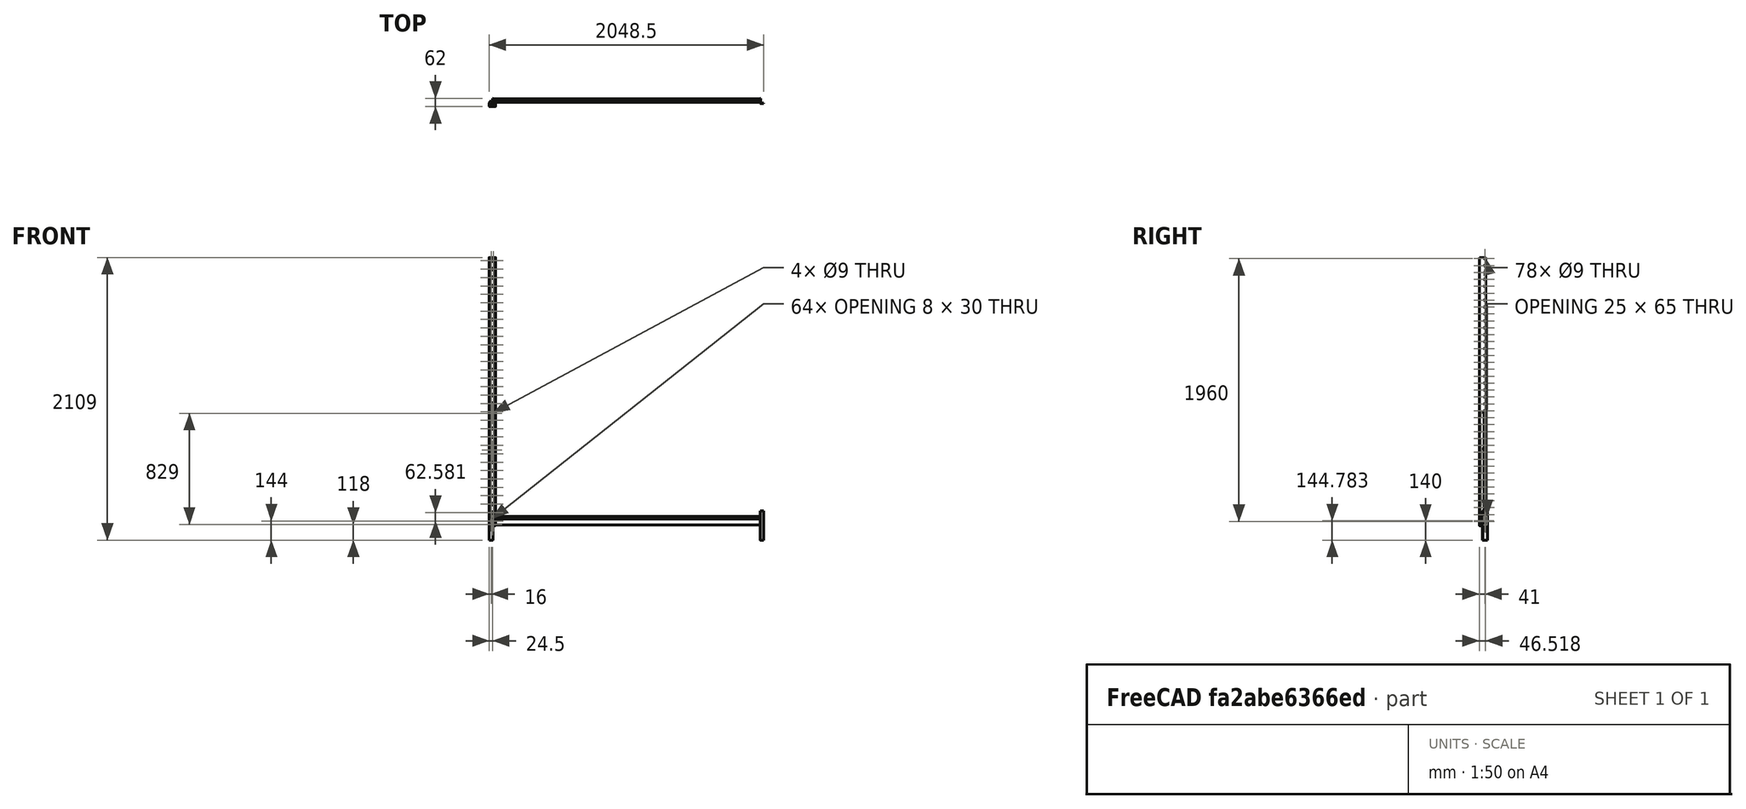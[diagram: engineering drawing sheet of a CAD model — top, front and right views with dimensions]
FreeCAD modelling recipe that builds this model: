
FCSTD DOCUMENT  (FreeCAD 0.21R33675 (Git))
Label: Rack
License: Public Domain
LicenseURL: https://en.wikipedia.org/wiki/Public_domain
objects: TechDraw::DrawViewDimension×12, Sketcher::SketchObject×11, TechDraw::DrawViewPart×8, PartDesign::Pocket×6, PartDesign::Pad×5, PartDesign::Body×4, PartDesign::Mirrored×2, PartDesign::LinearPattern×2, PartDesign::Thickness×1, TechDraw::DrawSVGTemplate×1, Image::ImagePlane×1, PartDesign::Plane×1, App::Part×1, TechDraw::DrawViewDetail×1, TechDraw::DrawPage×1
note: 68 computed .brp shape members not serialized (recipe doc carries the construction recipe); baked Part::Feature solids carry a one-line shape summary decoded from their .brp

FEATURE [Sketcher::SketchObject] Sketch
  FullyConstrained = true
  MapMode = 5
  Support = -> [XY_Plane001]
  sketch-geometry (13):
    g0: LineSegment StartX=-24.5 StartY=25 StartZ=0 EndX=24.5 EndY=25 EndZ=0
    g1: LineSegment StartX=24.5 StartY=25 StartZ=0 EndX=24.5 EndY=-25 EndZ=0
    g2: LineSegment StartX=24.5 StartY=-25 StartZ=0 EndX=-24.5 EndY=-25 EndZ=0
    g3: LineSegment StartX=-24.5 StartY=-25 StartZ=0 EndX=-24.5 EndY=25 EndZ=0
    g4: LineSegment StartX=-13 StartY=25 StartZ=0 EndX=-13 EndY=7 EndZ=0
    g5: LineSegment StartX=-14.0892 StartY=4.93614 StartZ=0 EndX=-23.4108 EndY=-1.43614 EndZ=0
    g6: LineSegment StartX=-24.5 StartY=-3.5 StartZ=0 EndX=-24.5 EndY=-22.5 EndZ=0
    g7: LineSegment StartX=-22 StartY=-25 StartZ=0 EndX=0 EndY=-25 EndZ=0
    g8: ArcOfCircle CenterX=-22 CenterY=-3.5 CenterZ=0 NormalX=0 NormalY=0 NormalZ=1 AngleXU=0 Radius=2.5 StartAngle=2.17043 EndAngle=3.14159
    g9: ArcOfCircle CenterX=-15.5 CenterY=7 CenterZ=0 NormalX=0 NormalY=0 NormalZ=1 AngleXU=0 Radius=2.5 StartAngle=5.31202 EndAngle=6.28319
    g10: ArcOfCircle CenterX=-22 CenterY=-22.5 CenterZ=0 NormalX=0 NormalY=0 NormalZ=1 AngleXU=0 Radius=2.5 StartAngle=3.14159 EndAngle=4.71239
    g11: LineSegment StartX=0 StartY=-25 StartZ=0 EndX=0 EndY=25 EndZ=0
    g12: LineSegment StartX=-13 StartY=25 StartZ=0 EndX=0 EndY=25 EndZ=0
  constraints (35):
    c: Coincident(g0,g1)
    c: Coincident(g1,g2)
    c: Coincident(g2,g3)
    c: Coincident(g3,g0)
    c: Horizontal(g0)
    c: Horizontal(g2)
    c: Vertical(g1)
    c: Vertical(g3)
    c: Symmetric(g0,g1,g-1)
    c: DistanceY(g1,g1) = 50
    c: DistanceX(g2,g2) = 49
    c: PointOnObject(g4,g0)
    c: Vertical(g4)
    c: PointOnObject(g6,g3)
    c: PointOnObject(g7,g2)
    c: PointOnObject(g7,g2)
    c: Vertical(g6)
    c: Tangent(g8,g5) = -1.5708
    c: Tangent(g8,g6) = -1.5708
    c: PointOnObject(g7,g-2)
    c: Tangent(g4,g9) = 1.5708
    c: Tangent(g5,g9) = 1.5708
    c: Tangent(g10,g7) = -1.5708
    c: Tangent(g10,g6) = -1.5708
    c: Coincident(g11,g7)
    c: PointOnObject(g11,g0)
    c: Vertical(g11)
    c: Coincident(g12,g4)
    c: Coincident(g12,g11)
    c: Equal(g10,g8)
    c: Equal(g8,g9)
    c: Diameter(g9) = 5
    c: DistanceX(g12,g12) = 13
    c: DistanceY(g6,g6) = 19
    c: DistanceY(g4,g4) = 18
FEATURE [PartDesign::Pad] Pad
  Direction = (0,0,1)
  Length = 2000
  Length2 = 10
  Profile = -> Sketch
  ReferenceAxis = -> Sketch [N_Axis]
  Refine = true
  Type = 0
FEATURE [PartDesign::Mirrored] Mirrored
  BaseFeature = -> Pad
  MirrorPlane = -> Sketch [V_Axis]
  Originals = -> [Pad]
  Refine = true
FEATURE [PartDesign::Thickness] Thickness
  Base = -> Mirrored [Face15,Face7,Face14]
  BaseFeature = -> Mirrored
  Intersection = false
  Join = 0
  Mode = 0
  Refine = true
  Reversed = true
  SupportTransform = false
  Value = 2
FEATURE [Sketcher::SketchObject] Sketch001
  FullyConstrained = true
  MapMode = 5
  Placement = pos=(0,-23,0) rot=(0,0.707107,0.707107;3.14159rad)
  Support = -> [Thickness]
  sketch-geometry (12):
    g0: LineSegment StartX=-4.5 StartY=40 StartZ=0 EndX=-4.5 EndY=10 EndZ=0
    g1: LineSegment StartX=-4.5 StartY=10 StartZ=0 EndX=-12.5 EndY=10 EndZ=0
    g2: LineSegment StartX=-12.5 StartY=10 StartZ=0 EndX=-11.5 EndY=21.9583 EndZ=0
    g3: LineSegment StartX=-11.5 StartY=21.9583 StartZ=0 EndX=-9.5 EndY=25.0334 EndZ=0
    g4: LineSegment StartX=-9.5 StartY=25.0334 StartZ=0 EndX=-8.5 EndY=40 EndZ=0
    g5: LineSegment StartX=-8.5 StartY=40 StartZ=0 EndX=-4.5 EndY=40 EndZ=0
    g6: LineSegment StartX=4.5 StartY=40 StartZ=0 EndX=4.5 EndY=10 EndZ=0
    g7: LineSegment StartX=4.5 StartY=10 StartZ=0 EndX=12.5 EndY=10 EndZ=0
    g8: LineSegment StartX=12.5 StartY=10 StartZ=0 EndX=11.5 EndY=21.9583 EndZ=0
    g9: LineSegment StartX=11.5 StartY=21.9583 StartZ=0 EndX=9.5 EndY=25.0334 EndZ=0
    g10: LineSegment StartX=9.5 StartY=25.0334 StartZ=0 EndX=8.5 EndY=40 EndZ=0
    g11: LineSegment StartX=8.5 StartY=40 StartZ=0 EndX=4.5 EndY=40 EndZ=0
  constraints (32):
    c: Vertical(g0)
    c: Coincident(g0,g1)
    c: Horizontal(g1)
    c: Coincident(g1,g2)
    c: Coincident(g2,g3)
    c: Coincident(g3,g4)
    c: Coincident(g4,g5)
    c: Coincident(g5,g0)
    c: Horizontal(g5)
    c: Coincident(g6,g7)
    c: Horizontal(g7)
    c: Coincident(g7,g8)
    c: Coincident(g8,g9)
    c: Coincident(g9,g10)
    c: Coincident(g10,g11)
    c: Coincident(g11,g6)
    c: Horizontal(g11)
    c: Symmetric(g6,g0,g-2)
    c: Symmetric(g0,g6,g-2)
    c: Equal(g1,g7)
    c: Symmetric(g2,g8,g-2)
    c: Symmetric(g3,g9,g-2)
    c: Equal(g11,g5)
    c: DistanceX(g11,g11) = 4
    c: DistanceY(g6,g6) = 30
    c: DistanceX(g7,g7) = 8
    c: Distance(g8) = 12
    c: DistanceX(g0,g6) = 9
    c: DistanceX(g6,g8) = 7
    c: Distance(g10) = 15
    c: DistanceX(g6,g9) = 5
    c: DistanceY(g-1,g6) = 10
FEATURE [TechDraw::DrawSVGTemplate] Template
  EditableTexts = Designed_by_Name=Sebastian Madrid; Drawing_number=Drawing number; FC-Date=Date; FC-SC=Scale; FC-SH=Sheet; FC-Title=Rack; Subtitle=Modelado con FreeCAD; Weight=Weight
  Height = 210
  Orientation = 1
  Template = <path>
  Width = 297
FEATURE [PartDesign::Pocket] Pocket
  BaseFeature = -> Thickness
  Direction = (0,-1,2e-16)
  Length = 2
  Length2 = 5
  Profile = -> Sketch001
  ReferenceAxis = -> Sketch001 [N_Axis]
  Refine = true
  Type = 0
FEATURE [PartDesign::LinearPattern] LinearPattern
  BaseFeature = -> Pocket
  Direction = -> Z_Axis001
  Length = 1940
  Occurrences = 32
  Originals = -> [Pocket]
  Refine = true
FEATURE [Sketcher::SketchObject] Sketch002
  ExternalGeometry = -> [LinearPattern]
  FullyConstrained = true
  MapMode = 5
  Placement = pos=(13,0,0) rot=(0.57735,0.57735,0.57735;2.0944rad)
  Support = -> [LinearPattern]
  sketch-geometry (1):
    g0: Circle CenterX=16 CenterY=9 CenterZ=0 NormalX=0 NormalY=0 NormalZ=1 AngleXU=0 Radius=4.5
  constraints (3):
    c: Diameter(g0) = 9
    c: DistanceY(g-3,g0) = 9
    c: DistanceX(g0,g-3) = 9
FEATURE [PartDesign::Pocket] Pocket001
  BaseFeature = -> LinearPattern
  Direction = (-1,0,0)
  Length = 5
  Length2 = 5
  Profile = -> Sketch002
  ReferenceAxis = -> Sketch002 [N_Axis]
  Refine = true
  Type = 1
FEATURE [PartDesign::LinearPattern] LinearPattern001
  BaseFeature = -> Pocket001
  Direction = -> Z_Axis001
  Length = 1960
  Occurrences = 39
  Originals = -> [Pocket001]
  Refine = true
FEATURE [PartDesign::Body] Body  label="Pilar"
  Group = -> [Sketch,Pad,Mirrored,Thickness,Sketch001,Pocket,LinearPattern,Sketch002,Pocket001,LinearPattern001]
  Origin = -> Origin001
  Placement = pos=(0,0,2000) rot=(0,1,0;3.14159rad)
  Tip = -> LinearPattern001
FEATURE [TechDraw::DrawViewPart] View
  CoarseView = false
  Direction = (0,0,1)
  Focus = 100
  HardHidden = false
  IsoCount = 0
  IsoHidden = false
  IsoVisible = false
  LockPosition = false
  Perspective = false
  Rotation = 0
  ScaleType = 0
  ScrubCount = 0
  SeamHidden = false
  SeamVisible = true
  SmoothHidden = false
  SmoothVisible = true
  Source = -> [Body]
  X = 39.6499
  XDirection = (1,0,0)
  Y = 168.987
FEATURE [TechDraw::DrawViewDimension] Dimension
  AngleOverride = false
  Arbitrary = false
  ArbitraryTolerances = false
  EqualTolerance = true
  ExtensionAngle = 0
  FormatSpec = %.2w
  FormatSpecOverTolerance = %+.2w
  FormatSpecUnderTolerance = %+.2w
  Inverted = false
  LineAngle = 0
  LockPosition = false
  MeasureType = 1
  OverTolerance = 0
  References2D = -> [View]
  Rotation = 0
  ScaleType = 0
  TheoreticalExact = false
  Type = 1
  UnderTolerance = 0
  X = -1.9334
  Y = -27.8717
FEATURE [TechDraw::DrawViewDimension] Dimension001
  AngleOverride = false
  Arbitrary = false
  ArbitraryTolerances = false
  EqualTolerance = true
  ExtensionAngle = 0
  FormatSpec = %.2w
  FormatSpecOverTolerance = %+.2w
  FormatSpecUnderTolerance = %+.2w
  Inverted = false
  LineAngle = 0
  LockPosition = false
  MeasureType = 1
  OverTolerance = 0
  References2D = -> [View]
  Rotation = 0
  ScaleType = 0
  TheoreticalExact = false
  Type = 2
  UnderTolerance = 0
  X = 31.3504
  Y = 0.842803
FEATURE [TechDraw::DrawViewDimension] Dimension002
  AngleOverride = false
  Arbitrary = false
  ArbitraryTolerances = false
  EqualTolerance = true
  ExtensionAngle = 0
  FormatSpec = %.2w
  FormatSpecOverTolerance = %+.2w
  FormatSpecUnderTolerance = %+.2w
  Inverted = false
  LineAngle = 0
  LockPosition = false
  MeasureType = 1
  OverTolerance = 0
  References2D = -> [View]
  Rotation = 0
  ScaleType = 0
  TheoreticalExact = false
  Type = 1
  UnderTolerance = 0
  X = 0
  Y = 27.5
FEATURE [TechDraw::DrawViewDimension] Dimension003
  AngleOverride = false
  Arbitrary = false
  ArbitraryTolerances = false
  EqualTolerance = true
  ExtensionAngle = 0
  FormatSpec = %.2w
  FormatSpecOverTolerance = %+.2w
  FormatSpecUnderTolerance = %+.2w
  Inverted = false
  LineAngle = 0
  LockPosition = false
  MeasureType = 1
  OverTolerance = 0
  References2D = -> [View]
  Rotation = 0
  ScaleType = 0
  TheoreticalExact = false
  Type = 1
  UnderTolerance = 0
  X = 0.159838
  Y = 35.412
FEATURE [Sketcher::SketchObject] Sketch003
  FullyConstrained = true
  MapMode = 5
  Support = -> [XY_Plane002]
  sketch-geometry (16):
    g0: LineSegment StartX=-19.5 StartY=11 StartZ=0 EndX=19.5 EndY=11 EndZ=0
    g1: LineSegment StartX=22 StartY=8.5 StartZ=0 EndX=22 EndY=-8.5 EndZ=0
    g2: LineSegment StartX=19.5 StartY=-11 StartZ=0 EndX=-19.5 EndY=-11 EndZ=0
    g3: LineSegment StartX=-22 StartY=-8.5 StartZ=0 EndX=-22 EndY=8.5 EndZ=0
    g4: ArcOfCircle CenterX=-19.5 CenterY=8.5 CenterZ=0 NormalX=0 NormalY=0 NormalZ=1 AngleXU=0 Radius=2.5 StartAngle=1.5708 EndAngle=3.14159
    g5: ArcOfCircle CenterX=19.5 CenterY=8.5 CenterZ=0 NormalX=0 NormalY=0 NormalZ=1 AngleXU=0 Radius=2.5 StartAngle=0 EndAngle=1.5708
    g6: ArcOfCircle CenterX=19.5 CenterY=-8.5 CenterZ=0 NormalX=0 NormalY=0 NormalZ=1 AngleXU=0 Radius=2.5 StartAngle=4.71239 EndAngle=6.28319
    g7: ArcOfCircle CenterX=-19.5 CenterY=-8.5 CenterZ=0 NormalX=0 NormalY=0 NormalZ=1 AngleXU=0 Radius=2.5 StartAngle=3.14159 EndAngle=4.71239
    g8: LineSegment StartX=-19.5 StartY=10 StartZ=0 EndX=19.5 EndY=10 EndZ=0
    g9: LineSegment StartX=21 StartY=8.5 StartZ=0 EndX=21 EndY=-8.5 EndZ=0
    g10: LineSegment StartX=19.5 StartY=-10 StartZ=0 EndX=-19.5 EndY=-10 EndZ=0
    g11: LineSegment StartX=-21 StartY=-8.5 StartZ=0 EndX=-21 EndY=8.5 EndZ=0
    g12: ArcOfCircle CenterX=-19.5 CenterY=8.5 CenterZ=0 NormalX=0 NormalY=0 NormalZ=1 AngleXU=0 Radius=1.5 StartAngle=1.5708 EndAngle=3.14159
    g13: ArcOfCircle CenterX=19.5 CenterY=8.5 CenterZ=0 NormalX=0 NormalY=0 NormalZ=1 AngleXU=0 Radius=1.5 StartAngle=7.24e-14 EndAngle=1.5708
    g14: ArcOfCircle CenterX=19.5 CenterY=-8.5 CenterZ=0 NormalX=0 NormalY=0 NormalZ=1 AngleXU=0 Radius=1.5 StartAngle=4.71239 EndAngle=6.28319
    g15: ArcOfCircle CenterX=-19.5 CenterY=-8.5 CenterZ=0 NormalX=0 NormalY=0 NormalZ=1 AngleXU=0 Radius=1.5 StartAngle=3.14159 EndAngle=4.71239
  constraints (37):
    c: Horizontal(g0)
    c: Horizontal(g2)
    c: Vertical(g1)
    c: Vertical(g3)
    c: Tangent(g0,g4) = 1.5708
    c: Tangent(g3,g4) = 1.5708
    c: Tangent(g0,g5) = 1.5708
    c: Tangent(g1,g5) = 1.5708
    c: Tangent(g1,g6) = 1.5708
    c: Tangent(g2,g6) = 1.5708
    c: Tangent(g2,g7) = 1.5708
    c: Tangent(g3,g7) = 1.5708
    c: DistanceY(g2,g0) = 22
    c: DistanceX(g3,g1) = 44
    c: Equal(g4,g7)
    c: Equal(g7,g6)
    c: Equal(g6,g5)
    c: Diameter(g4) = 5
    c: Symmetric(g4,g6,g-1)
    c: Horizontal(g8)
    c: Horizontal(g10)
    c: Vertical(g9)
    c: Vertical(g11)
    c: Tangent(g8,g12) = 1.5708
    c: Tangent(g11,g12) = 1.5708
    c: Tangent(g8,g13) = 1.5708
    c: Tangent(g9,g13) = 1.5708
    c: Tangent(g9,g14) = 1.5708
    c: Tangent(g10,g14) = 1.5708
    c: Tangent(g10,g15) = 1.5708
    c: Tangent(g11,g15) = 1.5708
    c: Equal(g12,g15)
    c: Equal(g15,g14)
    c: Equal(g14,g13)
    c: Coincident(g12,g4)
    c: Coincident(g6,g14)
    c: DistanceY(g8,g0) = 1
FEATURE [PartDesign::Pad] Pad001
  Direction = (0,0,1)
  Length = 572
  Length2 = 10
  Profile = -> Sketch003
  ReferenceAxis = -> Sketch003 [N_Axis]
  Refine = true
  Type = 0
FEATURE [Sketcher::SketchObject] Sketch004
  ExternalGeometry = -> [Pad001]
  FullyConstrained = true
  MapMode = 5
  Placement = pos=(0,11,0) rot=(0,0.707107,0.707107;3.14159rad)
  Support = -> [Pad001]
  sketch-geometry (2):
    g0: Circle CenterX=0 CenterY=9 CenterZ=0 NormalX=0 NormalY=0 NormalZ=1 AngleXU=0 Radius=4.5
    g1: Circle CenterX=0 CenterY=563 CenterZ=0 NormalX=0 NormalY=0 NormalZ=1 AngleXU=0 Radius=4.5
  constraints (6):
    c: PointOnObject(g0,g-2)
    c: PointOnObject(g1,g-2)
    c: DistanceY(g1,g-3) = 9
    c: DistanceY(g-1,g0) = 9
    c: Diameter(g0) = 9
    c: Equal(g0,g1)
FEATURE [PartDesign::Pocket] Pocket002
  BaseFeature = -> Pad001
  Direction = (0,-1,2e-16)
  Length = 5
  Length2 = 5
  Profile = -> Sketch004
  ReferenceAxis = -> Sketch004 [N_Axis]
  Refine = true
  Type = 0
FEATURE [Sketcher::SketchObject] Sketch005
  FullyConstrained = true
  MapMode = 5
  Support = -> [XY_Plane003]
  sketch-geometry (16):
    g0: LineSegment StartX=-19.5 StartY=11 StartZ=0 EndX=19.5 EndY=11 EndZ=0
    g1: LineSegment StartX=22 StartY=8.5 StartZ=0 EndX=22 EndY=-8.5 EndZ=0
    g2: LineSegment StartX=19.5 StartY=-11 StartZ=0 EndX=-19.5 EndY=-11 EndZ=0
    g3: LineSegment StartX=-22 StartY=-8.5 StartZ=0 EndX=-22 EndY=8.5 EndZ=0
    g4: ArcOfCircle CenterX=-19.5 CenterY=8.5 CenterZ=0 NormalX=0 NormalY=0 NormalZ=1 AngleXU=0 Radius=2.5 StartAngle=1.5708 EndAngle=3.14159
    g5: ArcOfCircle CenterX=-19.5 CenterY=-8.5 CenterZ=0 NormalX=0 NormalY=0 NormalZ=1 AngleXU=0 Radius=2.5 StartAngle=3.14159 EndAngle=4.71239
    g6: ArcOfCircle CenterX=19.5 CenterY=8.5 CenterZ=0 NormalX=0 NormalY=0 NormalZ=1 AngleXU=0 Radius=2.5 StartAngle=2e-16 EndAngle=1.5708
    g7: ArcOfCircle CenterX=19.5 CenterY=-8.5 CenterZ=0 NormalX=0 NormalY=0 NormalZ=1 AngleXU=0 Radius=2.5 StartAngle=4.71239 EndAngle=6.28319
    g8: LineSegment StartX=-19.5 StartY=10 StartZ=0 EndX=19.5 EndY=10 EndZ=0
    g9: LineSegment StartX=21 StartY=8.5 StartZ=0 EndX=21 EndY=-8.5 EndZ=0
    g10: LineSegment StartX=19.5 StartY=-10 StartZ=0 EndX=-19.5 EndY=-10 EndZ=0
    g11: LineSegment StartX=-21 StartY=-8.5 StartZ=0 EndX=-21 EndY=8.5 EndZ=0
    g12: ArcOfCircle CenterX=-19.5 CenterY=8.5 CenterZ=0 NormalX=0 NormalY=0 NormalZ=1 AngleXU=0 Radius=1.5 StartAngle=1.5708 EndAngle=3.14159
    g13: ArcOfCircle CenterX=19.5 CenterY=8.5 CenterZ=0 NormalX=0 NormalY=0 NormalZ=1 AngleXU=0 Radius=1.5 StartAngle=1.9e-15 EndAngle=1.5708
    g14: ArcOfCircle CenterX=19.5 CenterY=-8.5 CenterZ=0 NormalX=0 NormalY=0 NormalZ=1 AngleXU=0 Radius=1.5 StartAngle=4.71239 EndAngle=6.28319
    g15: ArcOfCircle CenterX=-19.5 CenterY=-8.5 CenterZ=0 NormalX=0 NormalY=0 NormalZ=1 AngleXU=0 Radius=1.5 StartAngle=3.14159 EndAngle=4.71239
  constraints (37):
    c: Horizontal(g0)
    c: Horizontal(g2)
    c: Vertical(g1)
    c: Vertical(g3)
    c: Tangent(g0,g4) = 1.5708
    c: Tangent(g3,g4) = 1.5708
    c: Tangent(g2,g5) = 1.5708
    c: Tangent(g3,g5) = 1.5708
    c: Tangent(g0,g6) = 1.5708
    c: Tangent(g1,g6) = 1.5708
    c: Tangent(g1,g7) = 1.5708
    c: Tangent(g2,g7) = 1.5708
    c: Equal(g4,g5)
    c: Equal(g5,g6)
    c: Equal(g6,g7)
    c: Symmetric(g4,g7,g-1)
    c: DistanceY(g2,g0) = 22
    c: Diameter(g6) = 5
    c: DistanceX(g3,g1) = 44
    c: Horizontal(g8)
    c: Horizontal(g10)
    c: Vertical(g9)
    c: Vertical(g11)
    c: Tangent(g8,g12) = 1.5708
    c: Tangent(g11,g12) = 1.5708
    c: Tangent(g8,g13) = 1.5708
    c: Tangent(g9,g13) = 1.5708
    c: Tangent(g9,g14) = 1.5708
    c: Tangent(g10,g14) = 1.5708
    c: Tangent(g10,g15) = 1.5708
    c: Tangent(g11,g15) = 1.5708
    c: Equal(g12,g13)
    c: Equal(g13,g14)
    c: Equal(g14,g15)
    c: Coincident(g12,g4)
    c: Coincident(g7,g14)
    c: DistanceY(g8,g0) = 1
FEATURE [PartDesign::Pad] Pad002
  Direction = (0,0,1)
  Length = 847
  Length2 = 10
  Profile = -> Sketch005
  ReferenceAxis = -> Sketch005 [N_Axis]
  Refine = true
  Type = 0
FEATURE [Sketcher::SketchObject] Sketch006
  ExternalGeometry = -> [Pad002]
  FullyConstrained = true
  MapMode = 5
  Placement = pos=(0,-11,0) rot=(1,0,0;1.5708rad)
  Support = -> [Pad002]
  sketch-geometry (2):
    g0: Circle CenterX=0 CenterY=9 CenterZ=0 NormalX=0 NormalY=0 NormalZ=1 AngleXU=0 Radius=4.5
    g1: Circle CenterX=0 CenterY=838 CenterZ=0 NormalX=0 NormalY=0 NormalZ=1 AngleXU=0 Radius=4.5
  constraints (6):
    c: PointOnObject(g0,g-2)
    c: Diameter(g0) = 9
    c: DistanceY(g-1,g0) = 9
    c: PointOnObject(g1,g-2)
    c: Equal(g1,g0)
    c: DistanceY(g1,g-3) = 9
FEATURE [PartDesign::Pocket] Pocket003
  BaseFeature = -> Pad002
  Direction = (0,1,-2e-16)
  Length = 5
  Length2 = 5
  Profile = -> Sketch006
  ReferenceAxis = -> Sketch006 [N_Axis]
  Refine = true
  Type = 0
FEATURE [Sketcher::SketchObject] Sketch007
  ExternalGeometry = -> [Pocket002]
  FullyConstrained = true
  MapMode = 5
  Placement = pos=(0,-11,0) rot=(1,0,0;1.5708rad)
  Support = -> [Pocket002]
  sketch-geometry (4):
    g0: LineSegment StartX=-18 StartY=572 StartZ=0 EndX=18 EndY=572 EndZ=0
    g1: LineSegment StartX=18 StartY=572 StartZ=0 EndX=18 EndY=0 EndZ=0
    g2: LineSegment StartX=18 StartY=0 StartZ=0 EndX=-18 EndY=4.9e-15 EndZ=0
    g3: LineSegment StartX=-18 StartY=4.9e-15 StartZ=0 EndX=-18 EndY=572 EndZ=0
  constraints (11):
    c: Coincident(g0,g1)
    c: Coincident(g1,g2)
    c: Coincident(g2,g3)
    c: Coincident(g3,g0)
    c: Horizontal(g0)
    c: Vertical(g1)
    c: Vertical(g3)
    c: PointOnObject(g0,g-8)
    c: PointOnObject(g1,g-7)
    c: Symmetric(g2,g1,g-2)
    c: DistanceX(g1,g-5) = 4
FEATURE [PartDesign::Pocket] Pocket004
  BaseFeature = -> Pocket002
  Direction = (0,1,-2e-16)
  Length = 5
  Length2 = 5
  Profile = -> Sketch007
  ReferenceAxis = -> Sketch007 [N_Axis]
  Refine = true
  Type = 0
FEATURE [PartDesign::Body] Body001  label="Travesano"
  Group = -> [Sketch003,Pad001,Sketch004,Pocket002,Sketch007,Pocket004]
  Origin = -> Origin002
  Tip = -> Pocket004
FEATURE [Sketcher::SketchObject] Sketch008
  ExternalGeometry = -> [Pocket003]
  FullyConstrained = true
  MapMode = 5
  Placement = pos=(0,11,0) rot=(0,0.707107,0.707107;3.14159rad)
  Support = -> [Pocket003]
  sketch-geometry (4):
    g0: LineSegment StartX=-18 StartY=847 StartZ=0 EndX=18 EndY=847 EndZ=0
    g1: LineSegment StartX=18 StartY=847 StartZ=0 EndX=18 EndY=0 EndZ=0
    g2: LineSegment StartX=18 StartY=0 StartZ=0 EndX=-18 EndY=-4.9e-15 EndZ=0
    g3: LineSegment StartX=-18 StartY=-4.9e-15 StartZ=0 EndX=-18 EndY=847 EndZ=0
  constraints (11):
    c: Coincident(g0,g1)
    c: Coincident(g1,g2)
    c: Coincident(g2,g3)
    c: Coincident(g3,g0)
    c: Horizontal(g0)
    c: Vertical(g1)
    c: Vertical(g3)
    c: PointOnObject(g0,g-5)
    c: PointOnObject(g1,g-8)
    c: Symmetric(g2,g1,g-2)
    c: DistanceX(g1,g-6) = 4
FEATURE [PartDesign::Pocket] Pocket005
  BaseFeature = -> Pocket003
  Direction = (0,-1,2e-16)
  Length = 5
  Length2 = 5
  Profile = -> Sketch008
  ReferenceAxis = -> Sketch008 [N_Axis]
  Refine = true
  Type = 0
FEATURE [PartDesign::Body] Body002  label="Diagonal"
  Group = -> [Sketch005,Pad002,Sketch006,Pocket003,Sketch008,Pocket005]
  Origin = -> Origin003
  Tip = -> Pocket005
FEATURE [TechDraw::DrawViewPart] View001
  CoarseView = false
  Direction = (0,-1,0)
  Focus = 100
  HardHidden = false
  IsoCount = 0
  IsoHidden = false
  IsoVisible = false
  LockPosition = false
  Perspective = false
  Rotation = 0
  Scale = 0.08
  ScaleType = 2
  ScrubCount = 0
  SeamHidden = false
  SeamVisible = true
  SmoothHidden = false
  SmoothVisible = true
  Source = -> [Body]
  X = 105.841
  XDirection = (1,0,0)
  Y = 113.024
FEATURE [TechDraw::DrawViewPart] View002
  CoarseView = false
  Direction = (0,0,1)
  Focus = 100
  HardHidden = false
  IsoCount = 0
  IsoHidden = false
  IsoVisible = false
  LockPosition = false
  Perspective = false
  Rotation = 0
  ScaleType = 0
  ScrubCount = 0
  SeamHidden = false
  SeamVisible = true
  SmoothHidden = false
  SmoothVisible = true
  Source = -> [Body001]
  X = 41.3386
  XDirection = (1,0,0)
  Y = 119.404
FEATURE [TechDraw::DrawViewPart] View003
  CoarseView = false
  Direction = (0,1,0)
  Focus = 100
  HardHidden = false
  IsoCount = 0
  IsoHidden = false
  IsoVisible = false
  LockPosition = false
  Perspective = false
  Rotation = 0
  Scale = 0.08
  ScaleType = 2
  ScrubCount = 0
  SeamHidden = false
  SeamVisible = true
  SmoothHidden = false
  SmoothVisible = true
  Source = -> [Body001]
  X = 62.3557
  XDirection = (-1,0,0)
  Y = 56.299
FEATURE [TechDraw::DrawViewPart] View004
  CoarseView = false
  Direction = (0,-1,0)
  Focus = 100
  HardHidden = false
  IsoCount = 0
  IsoHidden = false
  IsoVisible = false
  LockPosition = false
  Perspective = false
  Rotation = 0
  Scale = 0.08
  ScaleType = 2
  ScrubCount = 0
  SeamHidden = false
  SeamVisible = true
  SmoothHidden = false
  SmoothVisible = true
  Source = -> [Body002]
  X = 79.4959
  XDirection = (1,0,0)
  Y = 67.6379
FEATURE [TechDraw::DrawViewPart] View005
  CoarseView = false
  Direction = (-1,0,0)
  Focus = 100
  HardHidden = false
  IsoCount = 0
  IsoHidden = false
  IsoVisible = false
  LockPosition = false
  Perspective = false
  Rotation = 0
  Scale = 0.08
  ScaleType = 2
  ScrubCount = 0
  SeamHidden = false
  SeamVisible = true
  SmoothHidden = false
  SmoothVisible = true
  Source = -> [Body]
  X = 92.7889
  XDirection = (0,-1,0)
  Y = 113.452
FEATURE [TechDraw::DrawViewDimension] Dimension009
  AngleOverride = false
  Arbitrary = false
  ArbitraryTolerances = false
  EqualTolerance = true
  ExtensionAngle = 0
  FormatSpec = %.2w
  FormatSpecOverTolerance = %+.2w
  FormatSpecUnderTolerance = %+.2w
  Inverted = false
  LineAngle = 0
  LockPosition = false
  MeasureType = 1
  OverTolerance = 0
  References2D = -> [View002]
  Rotation = 0
  ScaleType = 0
  TheoreticalExact = false
  Type = 2
  UnderTolerance = 0
  X = -31.8696
  Y = 2.37248
FEATURE [TechDraw::DrawViewDimension] Dimension010
  AngleOverride = false
  Arbitrary = false
  ArbitraryTolerances = false
  EqualTolerance = true
  ExtensionAngle = 0
  FormatSpec = %.2w
  FormatSpecOverTolerance = %+.2w
  FormatSpecUnderTolerance = %+.2w
  Inverted = false
  LineAngle = 0
  LockPosition = false
  MeasureType = 1
  OverTolerance = 0
  References2D = -> [View002]
  Rotation = 0
  ScaleType = 0
  TheoreticalExact = false
  Type = 1
  UnderTolerance = 0
  X = -2.16787
  Y = -10.4633
FEATURE [Sketcher::SketchObject] Sketch009
  FullyConstrained = true
  MapMode = 5
  Support = -> [XY_Plane004]
  sketch-geometry (8):
    g0: LineSegment StartX=-24 StartY=0 StartZ=0 EndX=-4.5 EndY=0 EndZ=0
    g1: LineSegment StartX=0 StartY=37 StartZ=0 EndX=0 EndY=4.5 EndZ=0
    g2: ArcOfCircle CenterX=-4.5 CenterY=4.5 CenterZ=0 NormalX=0 NormalY=0 NormalZ=1 AngleXU=0 Radius=4.5 StartAngle=4.71239 EndAngle=6.28319
    g3: LineSegment StartX=-24 StartY=-3 StartZ=0 EndX=-4.5 EndY=-3 EndZ=0
    g4: LineSegment StartX=3 StartY=37 StartZ=0 EndX=3 EndY=4.5 EndZ=0
    g5: LineSegment StartX=-24 StartY=0 StartZ=0 EndX=-24 EndY=-3 EndZ=0
    g6: LineSegment StartX=0 StartY=37 StartZ=0 EndX=3 EndY=37 EndZ=0
    g7: ArcOfCircle CenterX=-4.5 CenterY=4.5 CenterZ=0 NormalX=0 NormalY=0 NormalZ=1 AngleXU=0 Radius=7.5 StartAngle=4.71239 EndAngle=6.28319
  constraints (21):
    c: PointOnObject(g0,g-1)
    c: PointOnObject(g0,g-1)
    c: PointOnObject(g1,g-2)
    c: PointOnObject(g1,g-2)
    c: Horizontal(g3)
    c: Vertical(g4)
    c: Coincident(g5,g0)
    c: Coincident(g5,g3)
    c: Coincident(g6,g1)
    c: Coincident(g6,g4)
    c: Horizontal(g6)
    c: Vertical(g5)
    c: Coincident(g7,g2)
    c: Tangent(g7,g4) = 1.5708
    c: Tangent(g7,g3) = -1.5708
    c: Tangent(g2,g1) = 1.5708
    c: Tangent(g2,g0) = -1.5708
    c: Diameter(g2) = 9
    c: DistanceX(g6,g6) = 3
    c: DistanceX(g3,g4) = 27
    c: DistanceY(g3,g4) = 40
FEATURE [PartDesign::Pad] Pad003
  Direction = (0,0,1)
  Length = 218
  Length2 = 10
  Midplane = true
  Profile = -> Sketch009
  ReferenceAxis = -> Sketch009 [N_Axis]
  Refine = true
  Type = 0
FEATURE [Image::ImagePlane] naranja
  Placement = pos=(0.33583,12.3115,25.8838) rot=(0.57735,0.57735,0.57735;2.0944rad)
  XSize = 405.689
  YSize = 280.36
FEATURE [Sketcher::SketchObject] MirroredSketch
  FullyConstrained = false
  Placement = pos=(3,42,-11) rot=(0.57735,0.57735,0.57735;2.0944rad)
  sketch-geometry (28):
    g0: LineSegment StartX=-29.982 StartY=79.2832 StartZ=0 EndX=-29.982 EndY=67.4112 EndZ=0
    g1: LineSegment StartX=-24.982 StartY=62.4112 StartZ=0 EndX=-12.982 EndY=62.4112 EndZ=0
    g2: LineSegment StartX=-10.8313 StartY=52.8974 StartZ=0 EndX=-21.6988 EndY=47.7194 EndZ=0
    g3: LineSegment StartX=-27.5789 StartY=38.4042 StartZ=0 EndX=-27.5789 EndY=30.0662 EndZ=0
    g4: LineSegment StartX=-7.982 StartY=17.2832 StartZ=0 EndX=-24.982 EndY=17.2832 EndZ=0
    g5: LineSegment StartX=-27.9608 StartY=28.1497 StartZ=0 EndX=-29.6001 EndY=24.1998 EndZ=0
    g6: ArcOfCircle CenterX=-24.982 CenterY=22.2832 CenterZ=0 NormalX=0 NormalY=0 NormalZ=1 AngleXU=0 Radius=5 StartAngle=2.74821 EndAngle=4.71239
    g7: ArcOfCircle CenterX=-24.982 CenterY=67.4112 CenterZ=0 NormalX=0 NormalY=0 NormalZ=1 AngleXU=0 Radius=5 StartAngle=3.14159 EndAngle=4.71239
    g8: ArcOfCircle CenterX=-12.982 CenterY=57.4112 CenterZ=0 NormalX=0 NormalY=0 NormalZ=1 AngleXU=0 Radius=5 StartAngle=5.15704 EndAngle=7.85398
    g9: ArcOfCircle CenterX=-17.2603 CenterY=38.4042 CenterZ=0 NormalX=0 NormalY=0 NormalZ=1 AngleXU=0 Radius=10.3186 StartAngle=2.01544 EndAngle=3.14159
    g10: ArcOfCircle CenterX=-32.5789 CenterY=30.0662 CenterZ=0 NormalX=0 NormalY=0 NormalZ=1 AngleXU=0 Radius=5 StartAngle=5.8898 EndAngle=6.28319
    g11: ArcOfCircle CenterX=-24.982 CenterY=67.4112 CenterZ=0 NormalX=0 NormalY=0 NormalZ=1 AngleXU=0 Radius=8 StartAngle=3.14159 EndAngle=4.71239
    g12: ArcOfCircle CenterX=-12.982 CenterY=57.4112 CenterZ=0 NormalX=0 NormalY=0 NormalZ=1 AngleXU=0 Radius=2 StartAngle=5.15704 EndAngle=7.85398
    g13: ArcOfCircle CenterX=-17.2603 CenterY=38.4042 CenterZ=0 NormalX=0 NormalY=0 NormalZ=1 AngleXU=0 Radius=13.3186 StartAngle=2.01544 EndAngle=3.14159
    g14: ArcOfCircle CenterX=-32.5789 CenterY=30.0662 CenterZ=0 NormalX=0 NormalY=0 NormalZ=1 AngleXU=0 Radius=2 StartAngle=5.8898 EndAngle=6.28319
    g15: ArcOfCircle CenterX=-24.982 CenterY=22.2832 CenterZ=0 NormalX=0 NormalY=0 NormalZ=1 AngleXU=0 Radius=8 StartAngle=2.74821 EndAngle=4.71239
    g16: LineSegment StartX=-7.982 StartY=17.2832 StartZ=0 EndX=-7.982 EndY=14.2832 EndZ=0
    g17: LineSegment StartX=-7.982 StartY=14.2832 StartZ=0 EndX=-24.982 EndY=14.2832 EndZ=0
    g18: LineSegment StartX=-32.3709 StartY=25.3497 StartZ=0 EndX=-30.7317 EndY=29.2996 EndZ=0
    g19: LineSegment StartX=-30.5789 StartY=38.4042 StartZ=0 EndX=-30.5789 EndY=30.0662 EndZ=0
    g20: LineSegment StartX=-12.1217 StartY=55.6057 StartZ=0 EndX=-22.9892 EndY=50.4277 EndZ=0
    g21: LineSegment StartX=-12.982 StartY=59.4112 StartZ=0 EndX=-24.982 EndY=59.4112 EndZ=0
    g22: LineSegment StartX=-32.982 StartY=67.4112 StartZ=0 EndX=-32.982 EndY=79.2832 EndZ=0
    g23: LineSegment StartX=-29.982 StartY=79.2832 StartZ=0 EndX=-32.982 EndY=79.2832 EndZ=0
    g24: LineSegment StartX=-7.982 StartY=79.2832 StartZ=0 EndX=-32.982 EndY=79.2832 EndZ=0
    g25: LineSegment StartX=-32.982 StartY=79.2832 StartZ=0 EndX=-32.982 EndY=14.2832 EndZ=0
    g26: LineSegment StartX=-32.982 StartY=14.2832 StartZ=0 EndX=-7.982 EndY=14.2832 EndZ=0
    g27: LineSegment StartX=-7.982 StartY=14.2832 StartZ=0 EndX=-7.982 EndY=79.2832 EndZ=0
  constraints (57):
    c: Vertical(g0)
    c: Vertical(g3)
    c: Horizontal(g4)
    c: Tangent(g6,g4) = 1.5708
    c: Tangent(g6,g5) = -1.5708
    c: Tangent(g10,g5) = 1.5708
    c: Tangent(g10,g3) = 1.5708
    c: Tangent(g9,g3) = -1.5708
    c: Tangent(g9,g2) = -1.5708
    c: Tangent(g8,g2) = 1.5708
    c: Tangent(g8,g1) = 1.5708
    c: Horizontal(g1)
    c: Tangent(g7,g0) = -1.5708
    c: Tangent(g7,g1) = -1.5708
    c: Equal(g8,g6)
    c: Equal(g6,g10)
    c: Equal(g10,g7)
    c: Coincident(g11,g7)
    c: Coincident(g12,g8)
    c: Coincident(g13,g9)
    c: Coincident(g14,g10)
    c: Coincident(g15,g6)
    c: Coincident(g4,g16)
    c: Vertical(g16)
    c: Coincident(g16,g17)
    c: Horizontal(g17)
    c: Parallel(g5,g18)
    c: Tangent(g17,g15) = 1.5708
    c: Tangent(g18,g15) = 1.5708
    c: Tangent(g18,g14) = -1.5708
    c: Vertical(g19)
    c: Tangent(g19,g14) = 1.5708
    c: Tangent(g19,g13) = -1.5708
    c: Parallel(g20,g2)
    c: Tangent(g20,g13) = -1.5708
    c: Tangent(g20,g12) = 1.5708
    c: Horizontal(g21)
    c: Tangent(g21,g12) = -1.5708
    c: Tangent(g21,g11) = 1.5708
    c: Vertical(g22)
    c: Tangent(g22,g11) = 1.5708
    c: Coincident(g23,g0)
    c: Coincident(g23,g22)
    c: Horizontal(g23)
    c: Coincident(g24,g25)
    c: Coincident(g25,g26)
    c: Coincident(g26,g27)
    c: Coincident(g27,g24)
    c: Horizontal(g24)
    c: Horizontal(g26)
    c: Vertical(g25)
    c: Vertical(g27)
    c: Coincident(g26,g16)
    c: Coincident(g22,g24)
    c: Tangent(g25,g15)
    c: Tangent(g8,g27)
    c: Diameter(g7) = 10
FEATURE [PartDesign::Pad] Pad004
  BaseFeature = -> Pad003
  Direction = (1,0,0)
  Length = 1997
  Length2 = 10
  Profile = -> MirroredSketch
  ReferenceAxis = -> MirroredSketch [N_Axis]
  Refine = true
  Type = 0
FEATURE [PartDesign::Plane] DatumPlane
  AttachmentOffset = pos=(0,0,1000) rot=(0,0,1;0rad)
  Length = 60
  MapMode = 5
  Placement = pos=(1000,-2.22e-13,2.22e-13) rot=(0.57735,0.57735,0.57735;2.0944rad)
  ResizeMode = 0
  Support = -> [YZ_Plane004]
  Width = 60
FEATURE [PartDesign::Mirrored] Mirrored001
  BaseFeature = -> Pad004
  MirrorPlane = -> DatumPlane
  Originals = -> [Pad003]
  Refine = true
FEATURE [PartDesign::Body] Body003  label="Naranja"
  Group = -> [Sketch009,Pad003,MirroredSketch,Pad004,DatumPlane,Mirrored001]
  Origin = -> Origin004
  Tip = -> Mirrored001
FEATURE [App::Part] Part  label="Pieza"
  Group = -> [Body,Body001,Body002,Body003]
  Origin = -> Origin
FEATURE [TechDraw::DrawViewDetail] Detail
  AnchorPoint = (0,-10,0)
  BaseView = -> View001
  CoarseView = false
  Direction = (0,-1,0)
  Focus = 100
  HardHidden = false
  IsoCount = 0
  IsoHidden = false
  IsoVisible = false
  LockPosition = false
  Perspective = false
  Radius = 100
  Reference = 1
  Rotation = 0
  Scale = 0.5
  ScaleType = 2
  ScrubCount = 0
  SeamHidden = false
  SeamVisible = true
  SmoothHidden = false
  SmoothVisible = true
  Source = -> [Body]
  X = 219.414
  XDirection = (1,0,0)
  Y = 131.92
FEATURE [TechDraw::DrawViewDimension] Dimension013
  AngleOverride = false
  Arbitrary = false
  ArbitraryTolerances = false
  EqualTolerance = true
  ExtensionAngle = 0
  FormatSpec = %.2w
  FormatSpecOverTolerance = %+.2w
  FormatSpecUnderTolerance = %+.2w
  Inverted = false
  LineAngle = 0
  LockPosition = false
  MeasureType = 1
  OverTolerance = 0
  References2D = -> [Detail]
  Rotation = 0
  ScaleType = 0
  TheoreticalExact = false
  Type = 1
  UnderTolerance = 0
  X = 17.7481
  Y = -10.4779
FEATURE [TechDraw::DrawViewDimension] Dimension014
  AngleOverride = false
  Arbitrary = false
  ArbitraryTolerances = false
  EqualTolerance = true
  ExtensionAngle = 0
  FormatSpec = %.2w
  FormatSpecOverTolerance = %+.2w
  FormatSpecUnderTolerance = %+.2w
  Inverted = false
  LineAngle = 0
  LockPosition = false
  MeasureType = 1
  OverTolerance = 0
  References2D = -> [Detail]
  Rotation = 0
  ScaleType = 0
  TheoreticalExact = false
  Type = 1
  UnderTolerance = 0
  X = -20.0534
  Y = -33.4527
FEATURE [TechDraw::DrawViewPart] View006
  CoarseView = false
  Direction = (0,-1,0)
  Focus = 100
  HardHidden = false
  IsoCount = 0
  IsoHidden = false
  IsoVisible = false
  LockPosition = false
  Perspective = false
  Rotation = 0
  Scale = 0.08
  ScaleType = 2
  ScrubCount = 0
  SeamHidden = false
  SeamVisible = true
  SmoothHidden = false
  SmoothVisible = true
  Source = -> [Body003]
  X = 203.496
  XDirection = (1,0,0)
  Y = 70.6818
FEATURE [TechDraw::DrawViewPart] View007
  CoarseView = false
  Direction = (1,0,0)
  Focus = 100
  HardHidden = false
  IsoCount = 0
  IsoHidden = false
  IsoVisible = false
  LockPosition = false
  Perspective = false
  Rotation = 0
  Scale = 0.08
  ScaleType = 2
  ScrubCount = 0
  SeamHidden = false
  SeamVisible = true
  SmoothHidden = false
  SmoothVisible = true
  Source = -> [Body003]
  X = 127.06
  XDirection = (0,1,0)
  Y = 42.0783
FEATURE [TechDraw::DrawViewDimension] Dimension016
  AngleOverride = false
  Arbitrary = false
  ArbitraryTolerances = false
  EqualTolerance = true
  ExtensionAngle = 0
  FormatSpec = %.2w
  FormatSpecOverTolerance = %+.2w
  FormatSpecUnderTolerance = %+.2w
  Inverted = false
  LineAngle = 0
  LockPosition = false
  MeasureType = 1
  OverTolerance = 0
  References2D = -> [View007]
  Rotation = 0
  ScaleType = 0
  TheoreticalExact = false
  Type = 2
  UnderTolerance = 0
  X = 5.81159
  Y = 2.5
FEATURE [TechDraw::DrawViewDimension] Dimension018
  AngleOverride = false
  Arbitrary = false
  ArbitraryTolerances = false
  EqualTolerance = true
  ExtensionAngle = 0
  FormatSpec = %.2w
  FormatSpecOverTolerance = %+.2w
  FormatSpecUnderTolerance = %+.2w
  Inverted = false
  LineAngle = 0
  LockPosition = false
  MeasureType = 1
  OverTolerance = 0
  References2D = -> [Detail]
  Rotation = 0
  ScaleType = 0
  TheoreticalExact = false
  Type = 2
  UnderTolerance = 0
  X = 35.0795
  Y = -19.7352
FEATURE [TechDraw::DrawViewDimension] Dimension019
  AngleOverride = false
  Arbitrary = false
  ArbitraryTolerances = false
  EqualTolerance = true
  ExtensionAngle = 0
  FormatSpec = %.2w
  FormatSpecOverTolerance = %+.2w
  FormatSpecUnderTolerance = %+.2w
  Inverted = false
  LineAngle = 0
  LockPosition = false
  MeasureType = 1
  OverTolerance = 0
  References2D = -> [Detail]
  Rotation = 0
  ScaleType = 0
  TheoreticalExact = false
  Type = 2
  UnderTolerance = 0
  X = -27.7762
  Y = 9.03987
FEATURE [TechDraw::DrawViewDimension] Dimension020
  AngleOverride = false
  Arbitrary = false
  ArbitraryTolerances = false
  EqualTolerance = true
  ExtensionAngle = 0
  FormatSpec = %.2w
  FormatSpecOverTolerance = %+.2w
  FormatSpecUnderTolerance = %+.2w
  Inverted = false
  LineAngle = 0
  LockPosition = false
  MeasureType = 1
  OverTolerance = 0
  References2D = -> [View003]
  Rotation = 0
  ScaleType = 0
  TheoreticalExact = false
  Type = 2
  UnderTolerance = 0
  X = -11.1585
  Y = 3.26722
FEATURE [TechDraw::DrawPage] Page  label="Plano"
  KeepUpdated = true
  NextBalloonIndex = 1
  ProjectionType = 0
  Template = -> Template
  Views = -> [View,Dimension,Dimension001,Dimension002,Dimension003,View001,Detail,View002,View003,View004,View005,Dimension009,Dimension010,Dimension013,Dimension014,View006,View007,Dimension016,Dimension018,Dimension019,Dimension020]
note: 1 file-system path scrubbed to <path> (originals preserved in the JSON sidecar)
